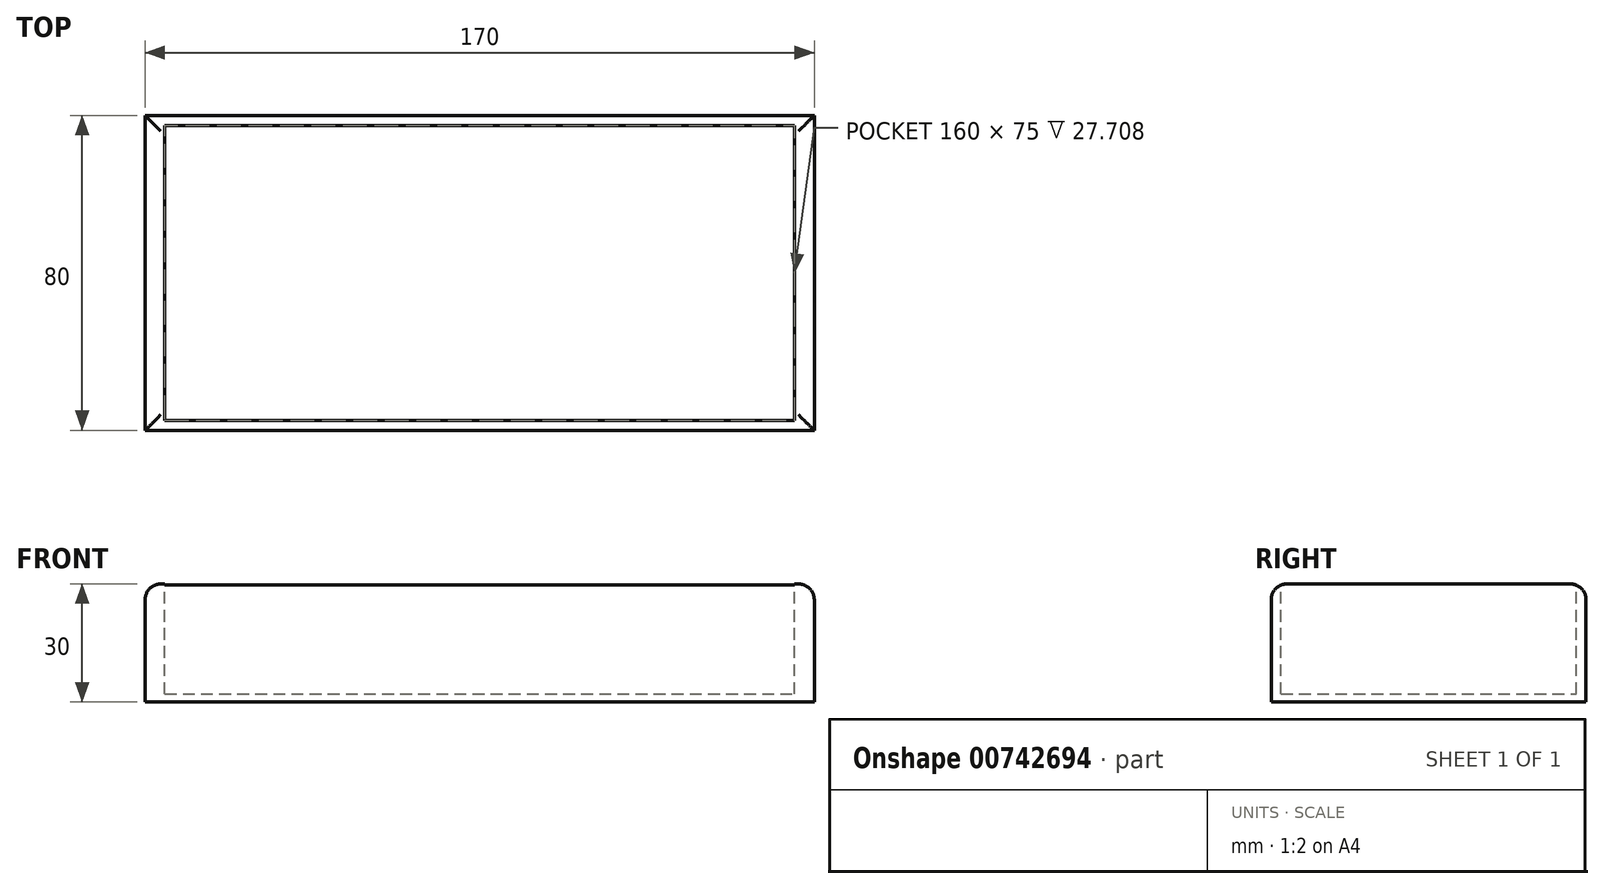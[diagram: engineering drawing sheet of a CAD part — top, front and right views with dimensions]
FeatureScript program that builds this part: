
annotation { "Feature Type Name" : "Feature", "Feature Type Description" : "" }
export const myFeature = defineFeature(function(context is Context, id is Id, definition is map)
    precondition{}
    {
        {
            var Q0;
            Q0=qCreatedBy(makeId("Top.planeOp"),FACE);
            var sketch = newSketch(context, id + "F0", { "sketchPlane" : qUnion([Q0])});
            skLineSegment(sketch, "E0.bottom", {"start": v(-85, -40) * mm, "end": v(85, -40) * mm});
            skLineSegment(sketch, "E0.top", {"start": v(-85, 40) * mm, "end": v(85, 40) * mm});
            skLineSegment(sketch, "E0.left", {"start": v(-85, -40) * mm, "end": v(-85, 40) * mm});
            skLineSegment(sketch, "E0.right", {"start": v(85, -40) * mm, "end": v(85, 40) * mm});
            skPoint(sketch, "E0.middle", {"position": v(0, 0) * mm});
            skSolve(sketch);
        }
        {
            var Q0;
            Q0 = qSketchRegion(id + "F0", true);
            extrude(context, id + "F1", {"entities" : qUnion([Q0]), "depth" : 30 * mm, "offsetDistance" : 25 * mm});
        }
        {
            var Q0;
            Q0=makeQuery(id+"F1.opExtrude","CAP_FACE",FACE,{"disambiguationData":[OSD([sQuery(id+"F0.wireOp",EDGE,"E0.bottom"),sQuery(id+"F0.wireOp",EDGE,"E0.top"),sQuery(id+"F0.wireOp",EDGE,"E0.left"),sQuery(id+"F0.wireOp",EDGE,"E0.right")])],"isStart":false});
            var sketch = newSketch(context, id + "F2", { "sketchPlane" : qUnion([Q0])});
            skLineSegment(sketch, "E1.bottom", {"start": v(-80, -37.5) * mm, "end": v(80, -37.5) * mm});
            skLineSegment(sketch, "E1.top", {"start": v(-80, 37.5) * mm, "end": v(80, 37.5) * mm});
            skLineSegment(sketch, "E1.left", {"start": v(-80, -37.5) * mm, "end": v(-80, 37.5) * mm});
            skLineSegment(sketch, "E1.right", {"start": v(80, -37.5) * mm, "end": v(80, 37.5) * mm});
            skPoint(sketch, "E1.middle", {"position": v(0, 0) * mm});
            skSolve(sketch);
        }
        {
            var Q0;
            Q0 = qSketchRegion(id + "F2", true);
            extrude(context, id + "F3", {"entities" : qUnion([Q0]), "operationType" : NewBodyOperationType.REMOVE, "depth" : -28 * mm, "offsetDistance" : 25 * mm});
        }
        {
            var Q0;
            Q0=makeQuery(id+"F1.opExtrude","CAP_EDGE",EDGE,{"disambiguationData":[OSD([sQuery(id+"F0.wireOp",EDGE,"E0.bottom")])],"isStart":false});
            var Q1;
            Q1=makeQuery(id+"F1.opExtrude","CAP_EDGE",EDGE,{"disambiguationData":[OSD([sQuery(id+"F0.wireOp",EDGE,"E0.left")])],"isStart":false});
            var Q2;
            Q2=makeQuery(id+"F1.opExtrude","CAP_EDGE",EDGE,{"disambiguationData":[OSD([sQuery(id+"F0.wireOp",EDGE,"E0.top")])],"isStart":false});
            var Q3;
            Q3=makeQuery(id+"F1.opExtrude","CAP_EDGE",EDGE,{"disambiguationData":[OSD([sQuery(id+"F0.wireOp",EDGE,"E0.right")])],"isStart":false});
            fillet(context, id + "F4", {"entities" : qUnion([Q0, Q1, Q2, Q3]), "radius" : 4 * mm, "tangentPropagation" : true, "allowEdgeOverflow" : false});
        }
    });
